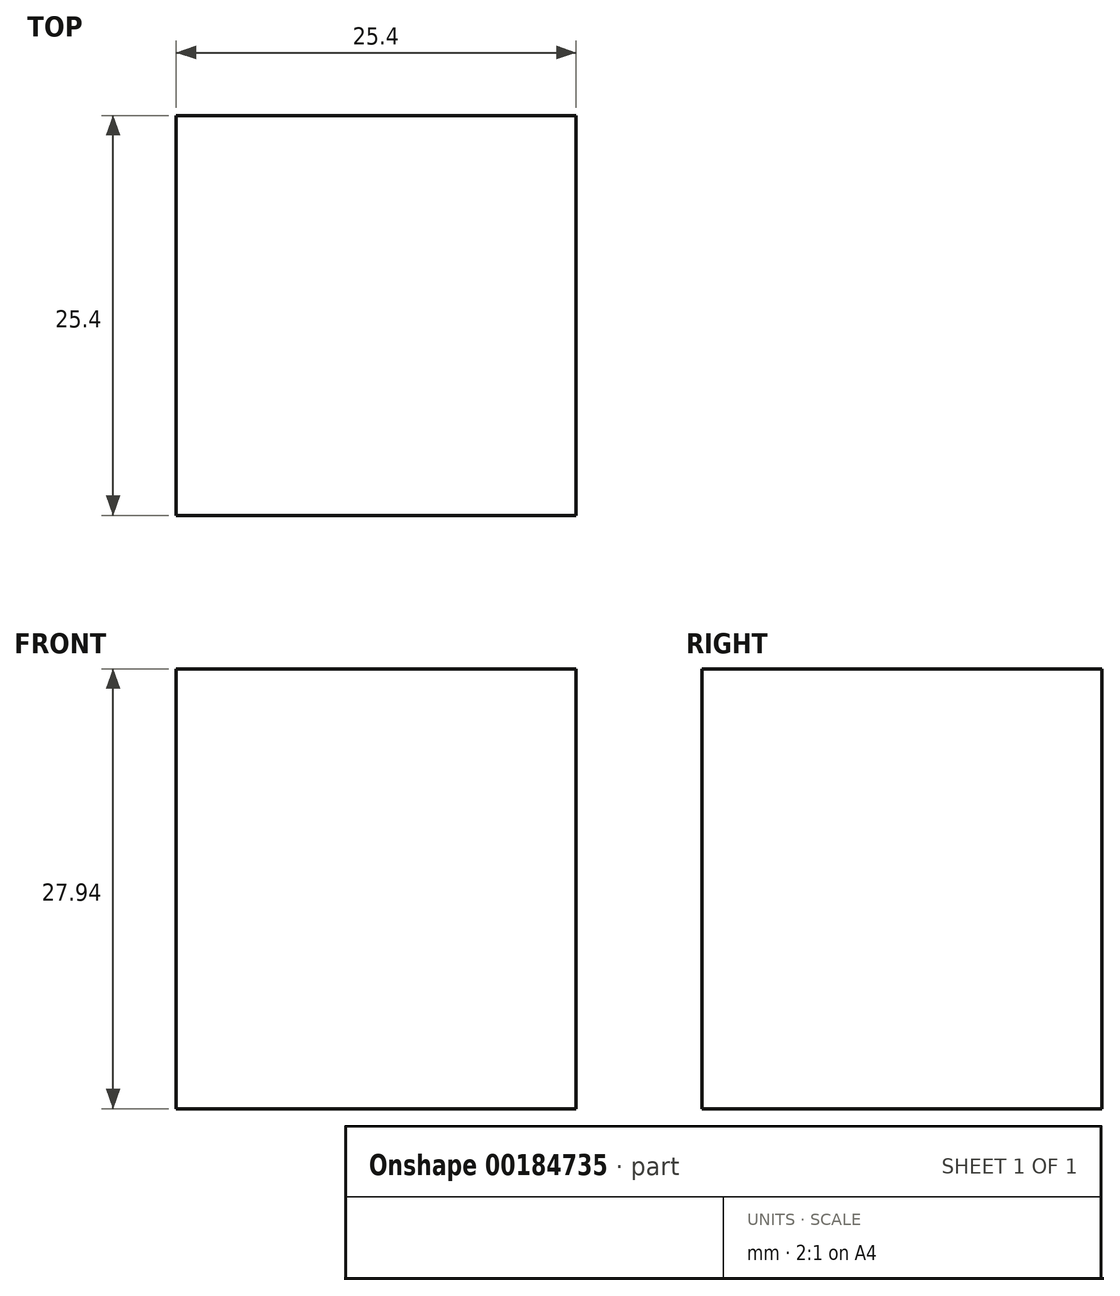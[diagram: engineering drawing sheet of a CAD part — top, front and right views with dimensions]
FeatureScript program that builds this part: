
annotation { "Feature Type Name" : "Feature", "Feature Type Description" : "" }
export const myFeature = defineFeature(function(context is Context, id is Id, definition is map)
    precondition{}
    {
        {
            var Q0;
            Q0=qCreatedBy(makeId("Top.planeOp"),FACE);
            var sketch = newSketch(context, id + "F0", { "sketchPlane" : qUnion([Q0])});
            skLineSegment(sketch, "E0.bottom", {"start": v(12.7, -12.7) * mm, "end": v(-12.7, -12.7) * mm});
            skLineSegment(sketch, "E0.top", {"start": v(12.7, 12.7) * mm, "end": v(-12.7, 12.7) * mm});
            skLineSegment(sketch, "E0.left", {"start": v(12.7, -12.7) * mm, "end": v(12.7, 12.7) * mm});
            skLineSegment(sketch, "E0.right", {"start": v(-12.7, -12.7) * mm, "end": v(-12.7, 12.7) * mm});
            skPoint(sketch, "E0.middle", {"position": v(0, 0) * mm});
            skSolve(sketch);
        }
        {
            var Q0;
            Q0 = qSketchRegion(id + "F0", true);
            extrude(context, id + "F1", {"entities" : qUnion([Q0]), "depth" : 27.94 * mm});
        }
    });
